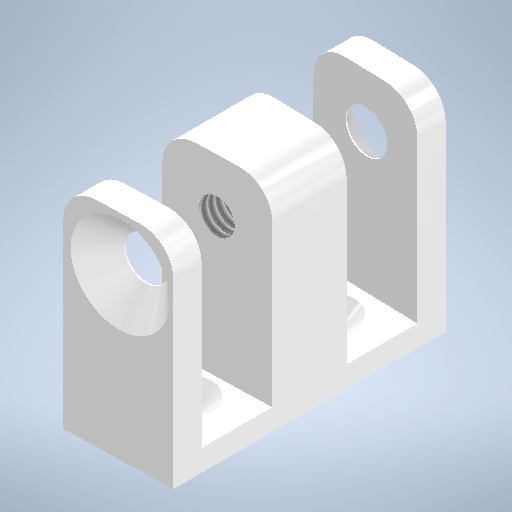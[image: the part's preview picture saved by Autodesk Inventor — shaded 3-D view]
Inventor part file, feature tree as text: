
AUTODESK INVENTOR PART (.ipt)
format: ipt  version: 2025 (Build 290162010, 162A)  size: 332,800 bytes
history: native  units: mm
features: sketch x7, hole x5, extrude x2, fillet x1, chamfer x1
ambient origin geometry x8: Origin, YZ Plane, XZ Plane, XY Plane, X Axis, Y Axis, Z Axis, Center Point
bodies: Volumenkörper1 (feature_tree)
feature tree (16):
  extrude  "Extrusion1"  Depth=3.0mm
  fillet  "Rundung1"  Radius=9.0mm
  sketch  "Skizze4"  dims[d37=13.333333mm d38=15.985064mm]
  extrude  "Extrusion3"  Depth=15.985064mm
  hole  "Bohrung4"  [1 undecoded]
  chamfer  "Fasen1"  Distance=2.0mm
  hole  "Bohrung5"  [1 undecoded]
  hole  "Bohrung6"  [1 undecoded]
  hole  "Bohrung7"  [1 undecoded]
  hole  "Bohrung8"  [1 undecoded]
  sketch  "Skizze1"  dims[d5=20.0mm d6=0.0mm d7=3.0mm d36=9.0mm]
  sketch  "Skizze6"  dims[d39=15.985064mm d40=10.0mm]
  sketch  "Skizze7"  dims[d41=6.6mm]
  sketch  "Skizze8"  dims[d42=6.6mm]
  sketch  "Skizze9"  dims[d43=13.83205mm d45=2.0mm d46=0.0mm]
  sketch  "Skizze10"  dims[d48=2.0mm d49=6.0mm d50=5.0mm d51=2.0mm d52=90.0deg d53=8.0mm d54=20.594885mm d55=1.5mm d56=2.0mm d57=45.0deg d58=26.0mm d59=13.333333mm d60=15.0mm d61=4.0mm d62=6.0mm d63=9.0mm d64=2.0mm d65=90.0deg d66=11.0mm d67=0.0mm d68=3.242mm d69=13.0mm d70=9.0mm d71=2.0mm d72=90.0deg d73=13.0mm d74=20.594885mm d75=15.0mm d76=4.0mm d77=12.0mm d78=9.0mm d79=2.0mm d80=90.0deg d81=13.0mm d82=0.0mm d83=3.242mm d84=13.0mm d85=9.0mm d86=2.0mm d87=90.0deg d88=13.0mm d89=20.594885mm]
note: 5 required parameter values undecoded (feature->parameter linkage not recoverable at this tier; creation-order binding heuristic only, values carry confidence <= 0.55)
